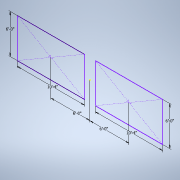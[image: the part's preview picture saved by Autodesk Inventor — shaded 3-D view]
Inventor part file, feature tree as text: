
AUTODESK INVENTOR PART (.ipt)
format: ipt  version: 2020.1 (Build 241239000, 239)  size: 93,696 bytes
history: native  units: in
note: dims shown in document units (in); Inventor stores cm internally (conversion verified against a paired STEP export)
features: sketch x1
ambient origin geometry x8: Origin, YZ Plane, XZ Plane, XY Plane, X Axis, Y Axis, Z Axis, Center Point
feature tree (1):
  sketch  "Sketch1"  dims[d0=72.0in d1=72.0in d2=124.0in d3=72.0in d4=124.0in d5=72.0in]
